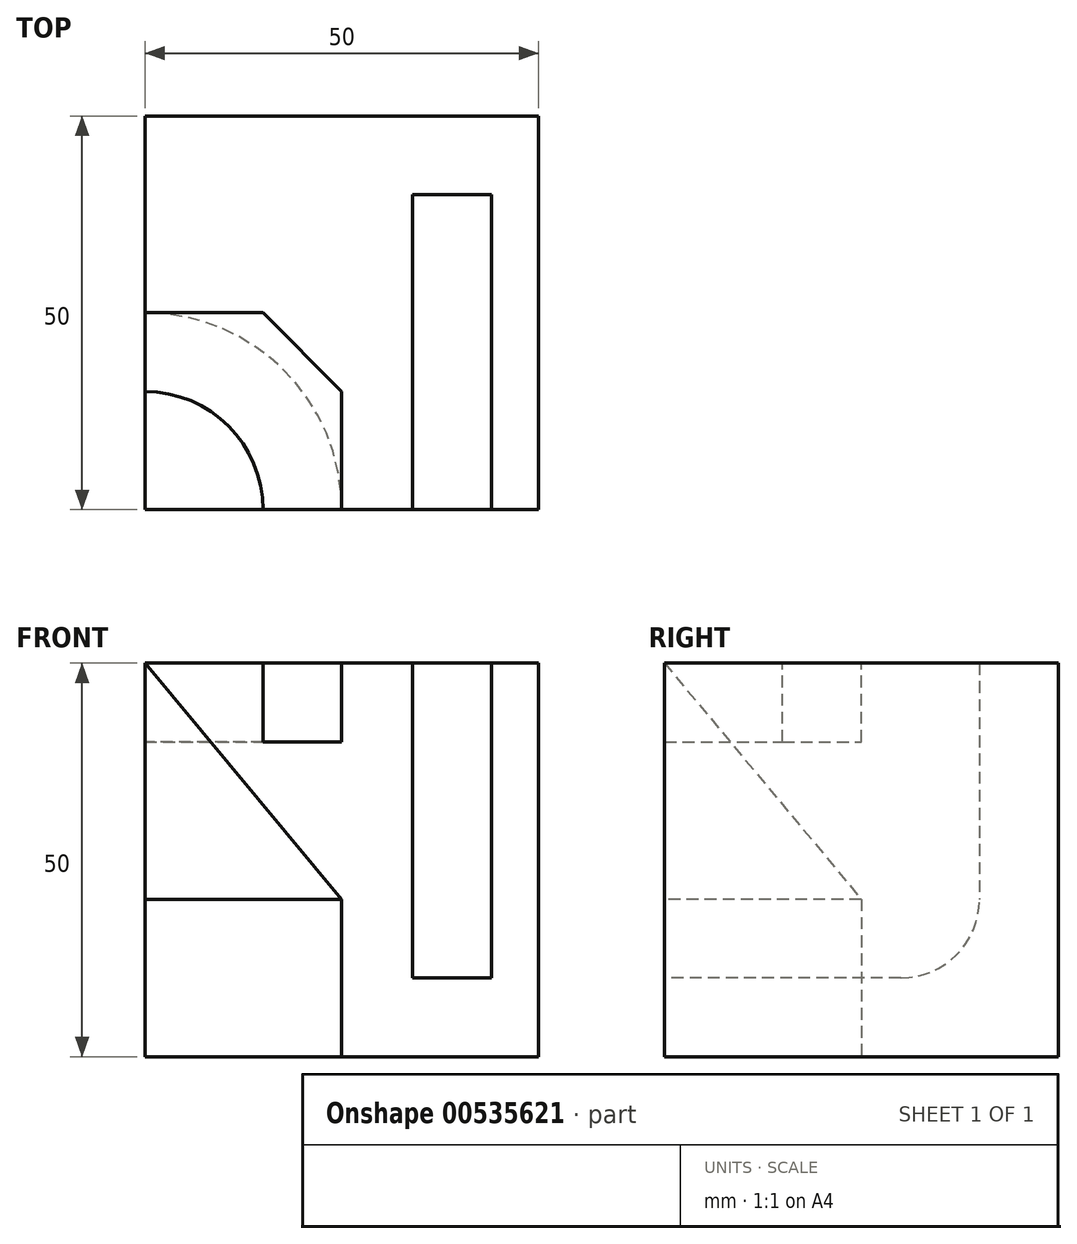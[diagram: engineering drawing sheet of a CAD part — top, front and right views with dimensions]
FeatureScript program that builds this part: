
annotation { "Feature Type Name" : "Feature", "Feature Type Description" : "" }
export const myFeature = defineFeature(function(context is Context, id is Id, definition is map)
    precondition{}
    {
        {
            var Q0;
            Q0=qCreatedBy(makeId("Top.planeOp"),FACE);
            var sketch = newSketch(context, id + "F0", { "sketchPlane" : qUnion([Q0])});
            skLineSegment(sketch, "E0.bottom", {"start": v(0, 0) * mm, "end": v(50, 0) * mm});
            skLineSegment(sketch, "E0.top", {"start": v(0, 50) * mm, "end": v(50, 50) * mm});
            skLineSegment(sketch, "E0.left", {"start": v(0, 0) * mm, "end": v(0, 50) * mm});
            skLineSegment(sketch, "E0.right", {"start": v(50, 0) * mm, "end": v(50, 50) * mm});
            skSolve(sketch);
        }
        {
            var Q0;
            Q0 = qSketchRegion(id + "F0", true);
            extrude(context, id + "F1", {"entities" : qUnion([Q0]), "depth" : 50 * mm, "offsetDistance" : 25 * mm});
        }
        {
            var Q0;
            Q0=makeQuery(id+"F1.opExtrude","CAP_FACE",FACE,{"disambiguationData":[OSD([sQuery(id+"F0.wireOp",EDGE,"E0.bottom"),sQuery(id+"F0.wireOp",EDGE,"E0.top"),sQuery(id+"F0.wireOp",EDGE,"E0.left"),sQuery(id+"F0.wireOp",EDGE,"E0.right")])],"isStart":false});
            var sketch = newSketch(context, id + "F2", { "sketchPlane" : qUnion([Q0])});
            skCircle(sketch, "E1", {"center": v(0, 0) * mm, "radius": 15 * mm});
            skLineSegment(sketch, "E2", {"start": v(0, 0) * mm, "end": v(0, 25) * mm});
            skLineSegment(sketch, "E3", {"start": v(0, 25) * mm, "end": v(15, 25) * mm});
            skLineSegment(sketch, "E4", {"start": v(0, 0) * mm, "end": v(25, 0) * mm});
            skLineSegment(sketch, "E5", {"start": v(25, 0) * mm, "end": v(25, 15) * mm});
            skLineSegment(sketch, "E6", {"start": v(25, 15) * mm, "end": v(15, 25) * mm});
            skSolve(sketch);
        }
        {
            var Q0;
            {var subQ0=sQuery(id+"F2.wireOp",EDGE,"E2");var subQ1=sQuery(id+"F2.wireOp",EDGE,"E1");var subQ2=makeQuery(id+"F2.imprint","INTERSECT",VERTEX,{"derivedFrom":[subQ1,subQ0]});Q0=makeQuery(id+"F2.imprint","IMPRINT",FACE,{"disambiguationData":[TD([[makeQuery(id+"F2.imprint","IMPRINT",EDGE,{"disambiguationData":[TD([[subQ2,-1.0]])],"derivedFrom":subQ1}),1.0]])]});}
            var Q1;
            {var subQ4=sQuery(id+"F2.wireOp",EDGE,"E3");Q1=makeQuery(id+"F2.imprint","IMPRINT",FACE,{"disambiguationData":[TD([[makeQuery(id+"F2.imprint","IMPRINT",EDGE,{"derivedFrom":subQ4}),-1.0]])]});}
            extrude(context, id + "F3", {"entities" : qUnion([Q0, Q1]), "operationType" : NewBodyOperationType.REMOVE, "oppositeDirection" : true, "depth" : 10 * mm, "offsetDistance" : 25 * mm});
        }
        {
            var Q0;
            Q0=makeQuery(id+"F1.opExtrude","CAP_FACE",FACE,{"disambiguationData":[OSD([sQuery(id+"F0.wireOp",EDGE,"E0.bottom"),sQuery(id+"F0.wireOp",EDGE,"E0.top"),sQuery(id+"F0.wireOp",EDGE,"E0.left"),sQuery(id+"F0.wireOp",EDGE,"E0.right")])],"isStart":true});
            var sketch = newSketch(context, id + "F4", { "sketchPlane" : qUnion([Q0])});
            skCircle(sketch, "E7", {"center": v(0, 0) * mm, "radius": 25 * mm});
            skSolve(sketch);
        }
        {
            var Q0;
            Q0 = qSketchRegion(id + "F4", true);
            extrude(context, id + "F5", {"entities" : qUnion([Q0]), "operationType" : NewBodyOperationType.REMOVE, "oppositeDirection" : true, "depth" : 20 * mm, "offsetDistance" : 25 * mm});
        }
        {
            var Q0;
            Q0=makeQuery(id+"F1.opExtrude","SWEPT_FACE",FACE,{"disambiguationData":[OSD([sQuery(id+"F0.wireOp",EDGE,"E0.bottom")])]});
            var sketch = newSketch(context, id + "F6", { "sketchPlane" : qUnion([Q0])});
            skLineSegment(sketch, "E8", {"start": v(0, 50) * mm, "end": v(25, 20) * mm});
            skLineSegment(sketch, "E9", {"start": v(0, 50) * mm, "end": v(0, 20) * mm});
            skLineSegment(sketch, "E10", {"start": v(25, 20) * mm, "end": v(0, 20) * mm});
            skSolve(sketch);
        }
        {
            var Q0;
            Q0=makeQuery(id+"F6.imprint","IMPRINT",FACE,{"disambiguationData":[TD([[makeQuery(id+"F6.imprint","IMPRINT",EDGE,{"derivedFrom":sQuery(id+"F6.wireOp",EDGE,"E8")}),-1.0]])]});
            var Q1;
            Q1=sQuery(id+"F6.wireOp",EDGE,"E9");
            revolve(context, id + "F7", {"operationType" : NewBodyOperationType.REMOVE, "entities" : qUnion([Q0]), "axis" : qUnion([Q1]), "revolveType" : RevolveType.FULL, "oppositeDirection" : true});
        }
        {
            var Q0;
            Q0=qCreatedBy(makeId("Right.planeOp"),FACE);
            cPlane(context, id + "F8", {"entities" : qUnion([Q0]), "cplaneType" : CPlaneType.OFFSET, "offset" : 34 * mm, "width" : 150 * mm, "height" : 150 * mm});
        }
        {
            var Q0;
            Q0=qCreatedBy(makeId("Right.planeOp"),FACE);
            cPlane(context, id + "F9", {"entities" : qUnion([Q0]), "cplaneType" : CPlaneType.OFFSET, "offset" : 44 * mm, "width" : 150 * mm, "height" : 150 * mm});
        }
        {
            var Q0;
            Q0=qCreatedBy(id+"F9.planeOp",FACE);
            var sketch = newSketch(context, id + "F10", { "sketchPlane" : qUnion([Q0])});
            skLineSegment(sketch, "E11", {"start": v(0, 0) * mm, "end": v(0, 10) * mm});
            skLineSegment(sketch, "E12", {"start": v(0, 10) * mm, "end": v(30, 10) * mm});
            skLineSegment(sketch, "E13", {"start": v(30, 10) * mm, "end": v(30, 20) * mm});
            skLineSegment(sketch, "E14", {"start": v(30, 20) * mm, "end": v(40, 20) * mm});
            skLineSegment(sketch, "E15", {"start": v(40, 20) * mm, "end": v(40, 50) * mm});
            skLineSegment(sketch, "E16", {"start": v(40, 50) * mm, "end": v(0, 50) * mm});
            skLineSegment(sketch, "E17", {"start": v(0, 50) * mm, "end": v(0, 10) * mm});
            skArc(sketch, "E18", {"start": v(30, 10) * mm, "mid": v(37.07, 12.93) * mm, "end": v(40, 20) * mm});
            skSolve(sketch);
        }
        {
            var Q0;
            Q0 = qSketchRegion(id + "F10", true);
            var Q1;
            Q1=qCreatedBy(id+"F8.planeOp",FACE);
            extrude(context, id + "F11", {"entities" : qUnion([Q0]), "operationType" : NewBodyOperationType.REMOVE, "endBound" : BoundingType.UP_TO_SURFACE, "oppositeDirection" : true, "depth" : 25 * mm, "endBoundEntityFace" : qUnion([Q1]), "offsetDistance" : 25 * mm});
        }
    });
